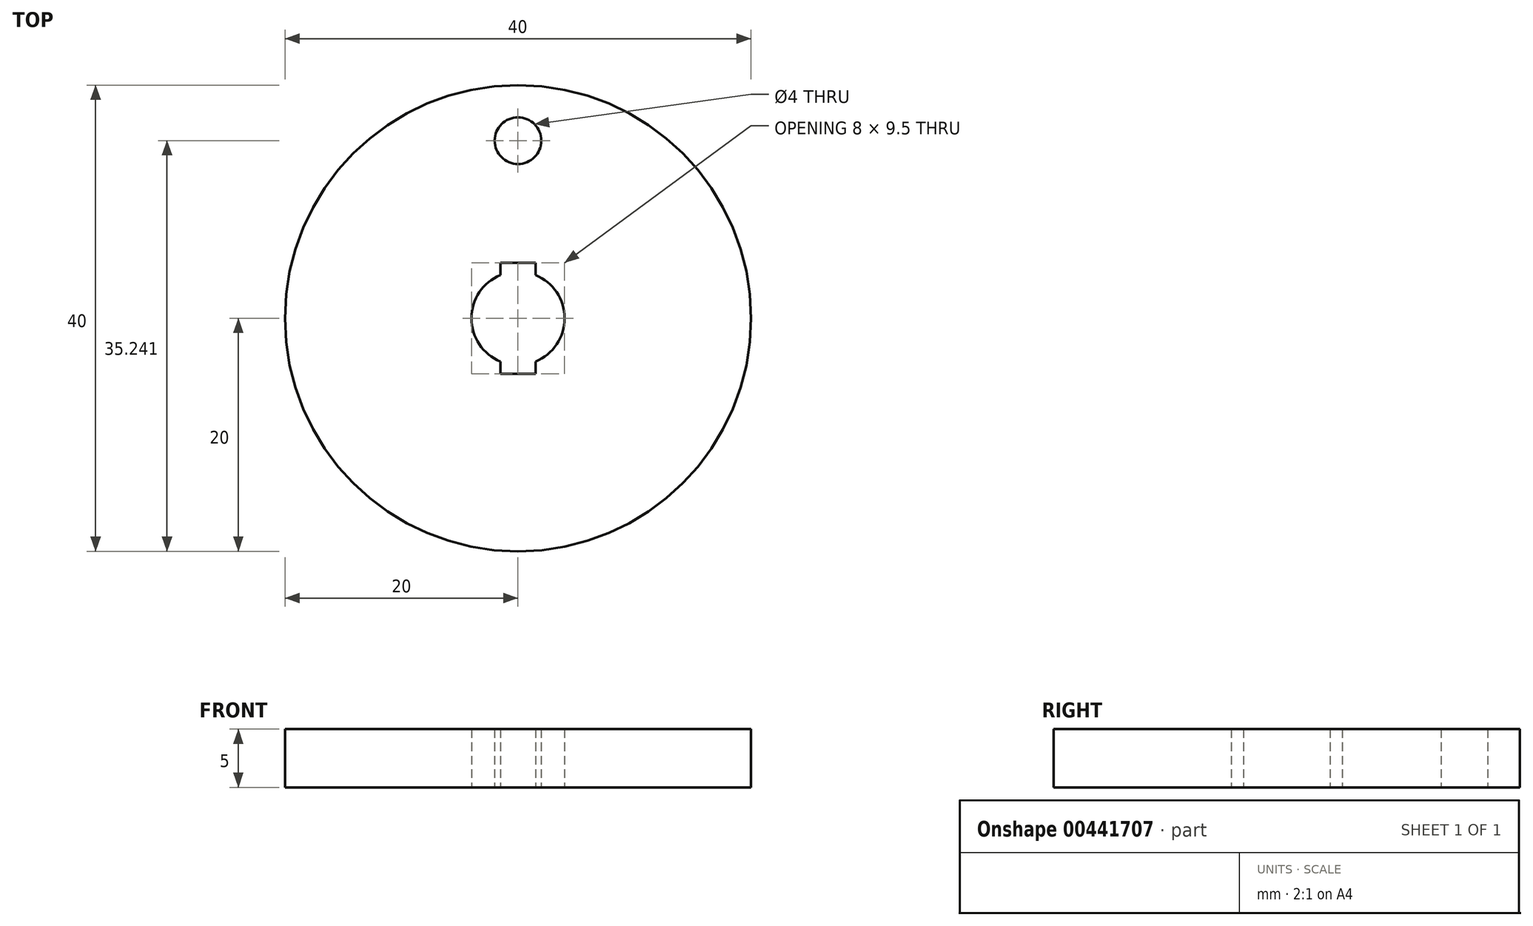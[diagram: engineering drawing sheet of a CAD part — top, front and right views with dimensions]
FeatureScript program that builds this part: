
annotation { "Feature Type Name" : "Feature", "Feature Type Description" : "" }
export const myFeature = defineFeature(function(context is Context, id is Id, definition is map)
    precondition{}
    {
        {
            var Q0;
            Q0=qCreatedBy(makeId("Top.planeOp"),FACE);
            var sketch = newSketch(context, id + "F0", { "sketchPlane" : qUnion([Q0])});
            skCircle(sketch, "E0", {"center": v(0, 0) * mm, "radius": 20 * mm});
            skCircle(sketch, "E1", {"center": v(0, 0) * mm, "radius": 4 * mm});
            skCircle(sketch, "E2", {"center": v(0, 15.24) * mm, "radius": 2 * mm});
            skLineSegment(sketch, "E3", {"start": v(0, 23.26) * mm, "end": v(0, -23.64) * mm, "construction": true});
            skLineSegment(sketch, "E4", {"start": v(-27.47, 0) * mm, "end": v(25.13, 0) * mm, "construction": true});
            skLineSegment(sketch, "E5.bottom", {"start": v(-1.5, 4.75) * mm, "end": v(1.5, 4.75) * mm});
            skLineSegment(sketch, "E5.top", {"start": v(-1.5, -4.75) * mm, "end": v(1.5, -4.75) * mm});
            skLineSegment(sketch, "E5.left", {"start": v(-1.5, 4.75) * mm, "end": v(-1.5, -4.75) * mm});
            skLineSegment(sketch, "E5.right", {"start": v(1.5, 4.75) * mm, "end": v(1.5, -4.75) * mm});
            skSolve(sketch);
        }
        {
            var Q0;
            Q0 = qSketchRegion(id + "F0", true);
            extrude(context, id + "F1", {"entities" : qUnion([Q0]), "endBound" : BoundingType.SYMMETRIC, "depth" : 5 * mm});
        }
    });
